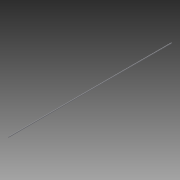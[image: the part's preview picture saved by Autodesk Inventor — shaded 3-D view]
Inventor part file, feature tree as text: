
AUTODESK INVENTOR PART (.ipt)
format: ipt  version: 2014 (Build 180170000, 170)  size: 62,464 bytes
history: native  units: in
note: dims shown in document units (in); Inventor stores cm internally (conversion verified against a paired STEP export)
features: extrude x1, sketch x1
ambient origin geometry x8: Origin, YZ Plane, XZ Plane, XY Plane, X Axis, Y Axis, Z Axis, Center Point
bodies: Solid1 (feature_tree)
feature tree (2):
  extrude  "Extrusion1"  Depth=50.0in TaperAngle=0.0deg
  sketch  "Sketch1"  dims[d0=0.25in d1=50.0in d2=0.0in]
